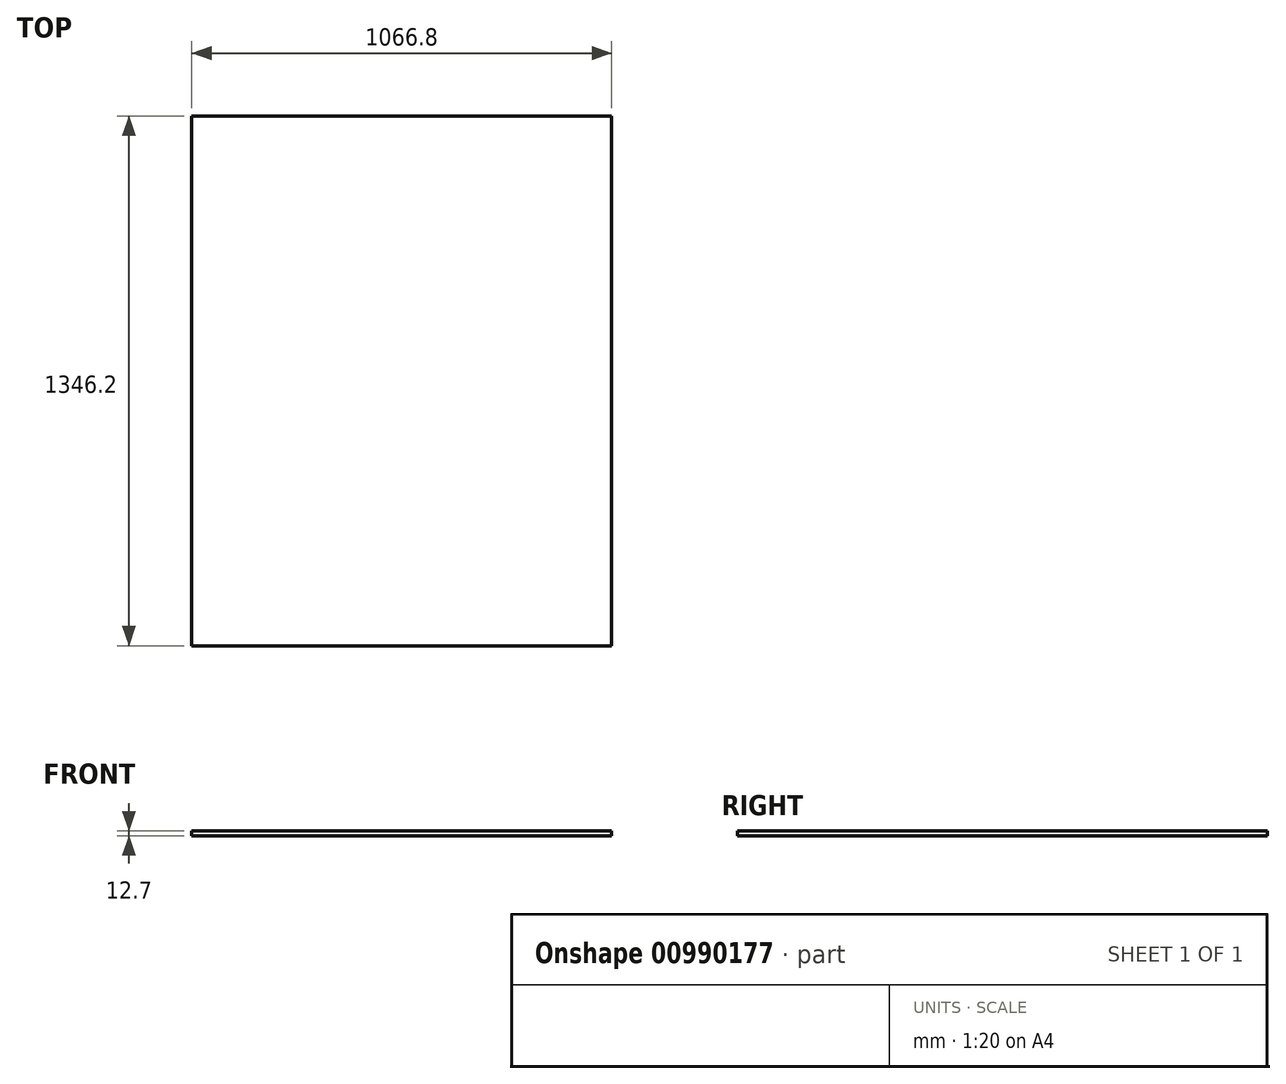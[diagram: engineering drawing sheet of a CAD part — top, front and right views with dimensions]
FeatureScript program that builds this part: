
annotation { "Feature Type Name" : "Feature", "Feature Type Description" : "" }
export const myFeature = defineFeature(function(context is Context, id is Id, definition is map)
    precondition{}
    {
        {
            var Q0;
            Q0=qCreatedBy(makeId("Top.planeOp"),FACE);
            var sketch = newSketch(context, id + "F0", { "sketchPlane" : qUnion([Q0])});
            skLineSegment(sketch, "E0.bottom", {"start": v(533.4, 673.1) * mm, "end": v(-533.4, 673.1) * mm});
            skLineSegment(sketch, "E0.top", {"start": v(533.4, -673.1) * mm, "end": v(-533.4, -673.1) * mm});
            skLineSegment(sketch, "E0.left", {"start": v(533.4, 673.1) * mm, "end": v(533.4, -673.1) * mm});
            skLineSegment(sketch, "E0.right", {"start": v(-533.4, 673.1) * mm, "end": v(-533.4, -673.1) * mm});
            skPoint(sketch, "E0.middle", {"position": v(0, 0) * mm});
            skSolve(sketch);
        }
        {
            var Q0;
            Q0 = qSketchRegion(id + "F0", true);
            extrude(context, id + "F1", {"entities" : qUnion([Q0]), "depth" : 12.7 * mm, "offsetDistance" : 25.4 * mm});
        }
    });
